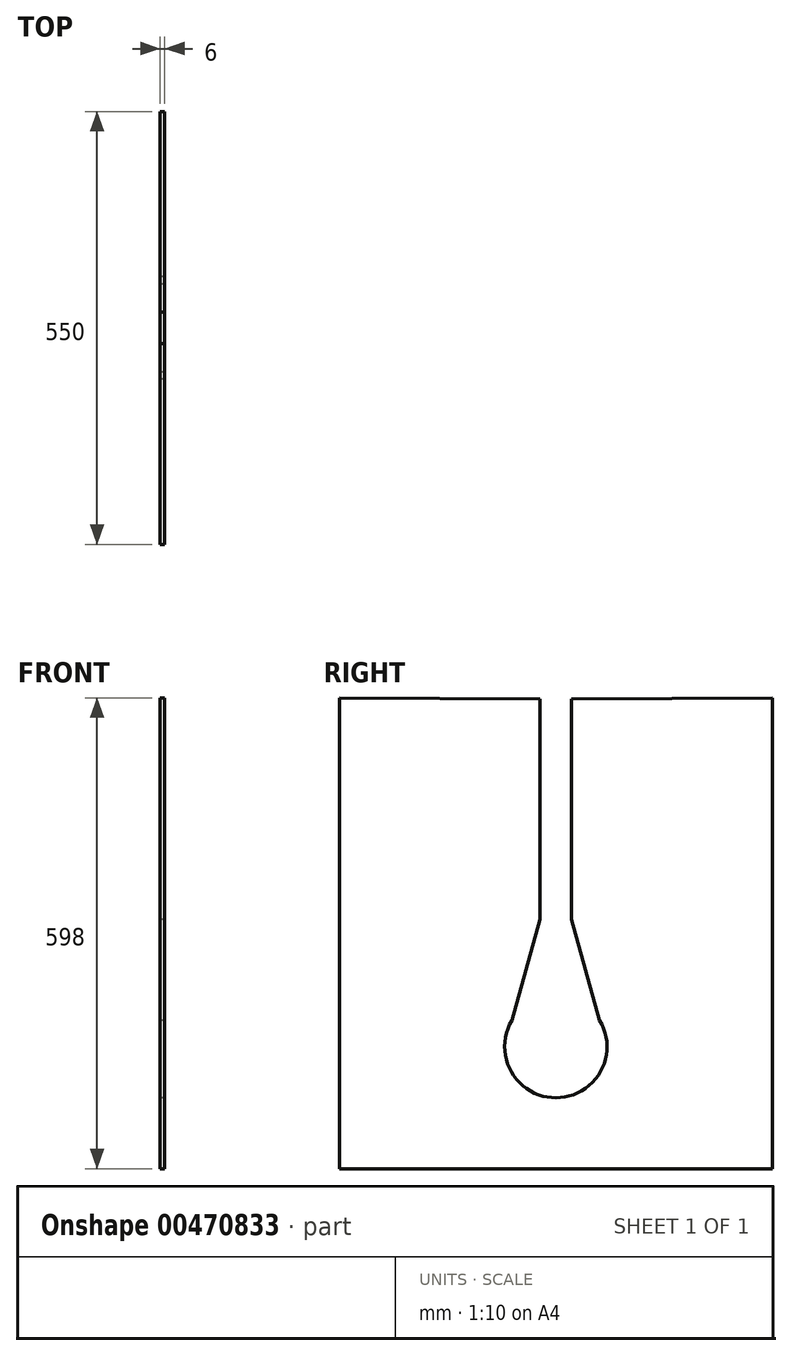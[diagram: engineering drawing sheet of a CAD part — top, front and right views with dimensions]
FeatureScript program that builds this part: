
annotation { "Feature Type Name" : "Feature", "Feature Type Description" : "" }
export const myFeature = defineFeature(function(context is Context, id is Id, definition is map)
    precondition{}
    {
        {
            var Q0;
            Q0=qCreatedBy(makeId("Right.planeOp"),FACE);
            var sketch = newSketch(context, id + "F0", { "sketchPlane" : qUnion([Q0])});
            skLineSegment(sketch, "E0.top", {"start": v(0, -23.96) * mm, "end": v(550, -23.96) * mm});
            skLineSegment(sketch, "E0.left", {"start": v(0, 574.04) * mm, "end": v(0, -23.96) * mm});
            skLineSegment(sketch, "E0.right", {"start": v(550, 574.04) * mm, "end": v(550, -23.96) * mm});
            skLineSegment(sketch, "E1", {"start": v(550, 574.04) * mm, "end": v(295, 572.8) * mm});
            skLineSegment(sketch, "E2", {"start": v(255, 572.8) * mm, "end": v(255, 192.89) * mm});
            skLineSegment(sketch, "E3", {"start": v(295, 572.8) * mm, "end": v(295, 192.89) * mm});
            skArc(sketch, "E4", {"start": v(255, 192.89) * mm, "mid": v(275, 66.04) * mm, "end": v(295, 192.89) * mm});
            skLineSegment(sketch, "E5", {"start": v(0, 574.04) * mm, "end": v(255, 572.8) * mm});
            skLineSegment(sketch, "E6", {"start": v(210, 131.52) * mm, "end": v(255, 292.8) * mm});
            skLineSegment(sketch, "E7", {"start": v(295, 292.8) * mm, "end": v(340, 130.94) * mm});
            skSolve(sketch);
        }
        {
            var Q0;
            Q0=makeQuery(id+"F0.imprint","IMPRINT",FACE,{"disambiguationData":[TD([[makeQuery(id+"F0.imprint","IMPRINT",EDGE,{"derivedFrom":sQuery(id+"F0.wireOp",EDGE,"E0.top")}),1.0]])]});
            extrude(context, id + "F1", {"entities" : qUnion([Q0]), "depth" : 6 * mm});
        }
    });
